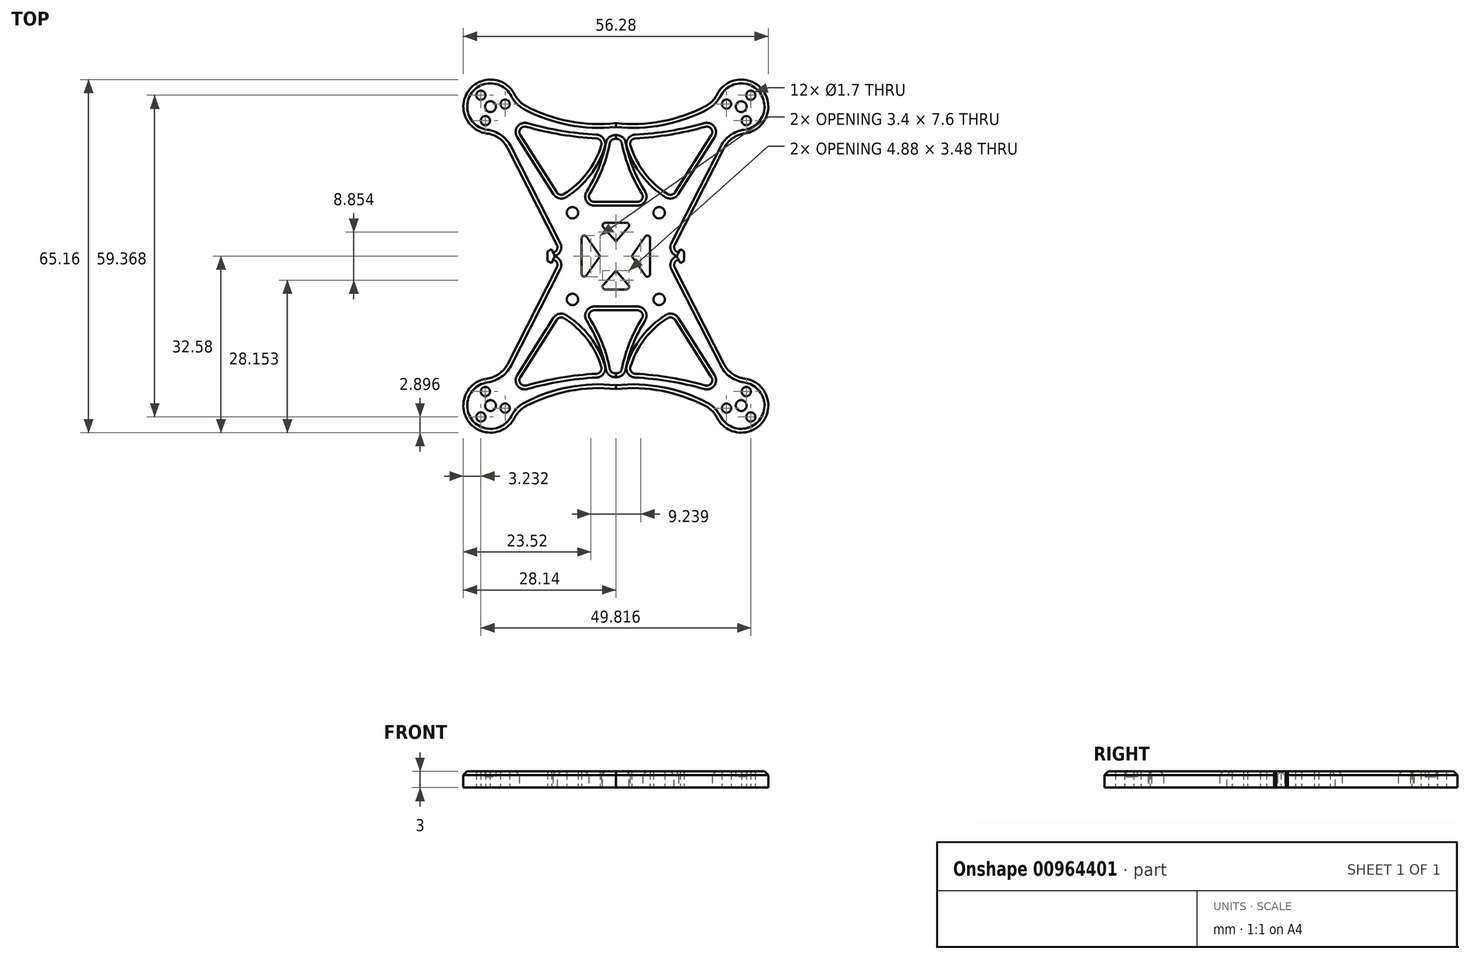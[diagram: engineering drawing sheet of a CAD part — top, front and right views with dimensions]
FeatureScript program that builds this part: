
annotation { "Feature Type Name" : "Feature", "Feature Type Description" : "" }
export const myFeature = defineFeature(function(context is Context, id is Id, definition is map)
    precondition{}
    {
        {
            var Q0;
            Q0=qCreatedBy(makeId("Top.planeOp"),FACE);
            var sketch = newSketch(context, id + "F0", { "sketchPlane" : qUnion([Q0])});
            skCircle(sketch, "E0", {"center": v(0, 0) * mm, "radius": 36 * mm, "construction": true});
            skLineSegment(sketch, "E1.bottom", {"start": v(8, -8) * mm, "end": v(-8, -8) * mm, "construction": true});
            skLineSegment(sketch, "E1.top", {"start": v(8, 8) * mm, "end": v(-8, 8) * mm, "construction": true});
            skLineSegment(sketch, "E1.left", {"start": v(8, -8) * mm, "end": v(8, 8) * mm, "construction": true});
            skLineSegment(sketch, "E1.right", {"start": v(-8, -8) * mm, "end": v(-8, 8) * mm, "construction": true});
            skCircle(sketch, "E2", {"center": v(-8, 8) * mm, "radius": 1.05 * mm});
            skCircle(sketch, "E3", {"center": v(8, 8) * mm, "radius": 1.05 * mm});
            skCircle(sketch, "E4", {"center": v(-8, -8) * mm, "radius": 1.05 * mm});
            skCircle(sketch, "E5", {"center": v(8, -8) * mm, "radius": 1.05 * mm});
            skLineSegment(sketch, "E6", {"start": v(0, 0) * mm, "end": v(50.6, 60.3) * mm, "construction": true});
            skPoint(sketch, "E7", {"position": v(23.14, 27.58) * mm});
            skCircle(sketch, "E8", {"center": v(23.14, 27.58) * mm, "radius": 1 * mm});
            skPoint(sketch, "E9", {"position": v(24.9, 29.68) * mm});
            skCircle(sketch, "E10", {"center": v(24.9, 29.68) * mm, "radius": 0.85 * mm});
            skCircle(sketch, "E11.1.0", {"center": v(20.43, 28.06) * mm, "radius": 0.85 * mm});
            skCircle(sketch, "E11.2.0", {"center": v(24.08, 25) * mm, "radius": 0.85 * mm});
            skCircle(sketch, "E12", {"center": v(23.14, 27.58) * mm, "radius": 20 * mm, "construction": true});
            skLineSegment(sketch, "E13.bottom", {"start": v(9.8, -10) * mm, "end": v(-9.8, -10) * mm});
            skLineSegment(sketch, "E13.top", {"start": v(9.8, 10) * mm, "end": v(-9.8, 10) * mm});
            skLineSegment(sketch, "E13.left", {"start": v(9.8, -10) * mm, "end": v(9.8, 10) * mm});
            skCircle(sketch, "E14", {"center": v(21.43, 25.54) * mm, "radius": 1.5 * mm, "construction": true});
            skLineSegment(sketch, "E15", {"start": v(23.14, 27.58) * mm, "end": v(9.8, 1.47) * mm, "construction": true});
            skLineSegment(sketch, "E16", {"start": v(9.8, 0) * mm, "end": v(22.09, 24.04) * mm});
            skCircle(sketch, "E17", {"center": v(23.14, 27.58) * mm, "radius": 5 * mm});
            skLineSegment(sketch, "E18", {"start": v(19.54, 25.37) * mm, "end": v(9.8, 10) * mm});
            skLineSegment(sketch, "E19", {"start": v(0, 10) * mm, "end": v(0, 0) * mm});
            skLineSegment(sketch, "E20", {"start": v(9.8, 0) * mm, "end": v(0, 0) * mm});
            skArc(sketch, "E21", {"start": v(0, 24.53) * mm, "mid": v(9.47, 25.07) * mm, "end": v(18.25, 28.64) * mm});
            skArc(sketch, "E22", {"start": v(0, 21.63) * mm, "mid": v(9.67, 22.35) * mm, "end": v(19.09, 24.65) * mm});
            skArc(sketch, "E23", {"start": v(2.36, 21.66) * mm, "mid": v(5.23, 15.44) * mm, "end": v(10.4, 10.96) * mm});
            skArc(sketch, "E24", {"start": v(0.97, 21.63) * mm, "mid": v(2.73, 15.53) * mm, "end": v(5.86, 10) * mm});
            skLineSegment(sketch, "E25", {"start": v(0, 24.53) * mm, "end": v(0, 21.63) * mm});
            skLineSegment(sketch, "E26", {"start": v(10.14, 0.66) * mm, "end": v(11.58, 0.66) * mm});
            skLineSegment(sketch, "E27", {"start": v(11.58, 0.66) * mm, "end": v(11.88, 1.25) * mm});
            skLineSegment(sketch, "E28", {"start": v(11.88, 1.25) * mm, "end": v(12.6, 0.88) * mm});
            skLineSegment(sketch, "E29", {"start": v(12.6, 0.88) * mm, "end": v(12.6, 0) * mm});
            skLineSegment(sketch, "E30", {"start": v(12.6, 0) * mm, "end": v(9.8, 0) * mm});
            skLineSegment(sketch, "E31", {"start": v(6.32, 4.9) * mm, "end": v(2.92, 0) * mm});
            skLineSegment(sketch, "E32", {"start": v(6.32, 4.9) * mm, "end": v(6.32, 0) * mm});
            skLineSegment(sketch, "E33", {"start": v(0, 6.17) * mm, "end": v(3.05, 6.17) * mm});
            skLineSegment(sketch, "E34", {"start": v(3.05, 6.17) * mm, "end": v(0, 2.69) * mm});
            skSolve(sketch);
        }
        {
            var Q0;
            {var subQ3=sQuery(id+"F0.wireOp",EDGE,"E21");Q0=makeQuery(id+"F0.imprint","IMPRINT",FACE,{"disambiguationData":[TD([[makeQuery(id+"F0.imprint","IMPRINT",EDGE,{"derivedFrom":subQ3}),-1.0]])]});}
            var Q1;
            Q1=makeQuery(id+"F0.imprint","IMPRINT",FACE,{"disambiguationData":[TD([[makeQuery(id+"F0.imprint","IMPRINT",EDGE,{"derivedFrom":sQuery(id+"F0.wireOp",EDGE,"E8")}),-1.0]])]});
            var Q2;
            {var subQ0=sQuery(id+"F0.wireOp",EDGE,"E17");var subQ1=sQuery(id+"F0.wireOp",EDGE,"E16");var subQ2=makeQuery(id+"F0.imprint","INTERSECT",VERTEX,{"derivedFrom":[subQ1,subQ0]});Q2=makeQuery(id+"F0.imprint","IMPRINT",FACE,{"disambiguationData":[TD([[makeQuery(id+"F0.imprint","IMPRINT",EDGE,{"disambiguationData":[TD([[subQ2,1.0]])],"derivedFrom":subQ0}),-1.0]])]});}
            var Q3;
            {var subQ0=sQuery(id+"F0.wireOp",EDGE,"E23");Q3=makeQuery(id+"F0.imprint","IMPRINT",FACE,{"disambiguationData":[TD([[makeQuery(id+"F0.imprint","IMPRINT",EDGE,{"derivedFrom":subQ0}),-1.0]])]});}
            var Q4;
            Q4=makeQuery(id+"F0.imprint","IMPRINT",FACE,{"disambiguationData":[TD([[makeQuery(id+"F0.imprint","IMPRINT",EDGE,{"derivedFrom":sQuery(id+"F0.wireOp",EDGE,"E3")}),-1.0]])]});
            var Q5;
            {var subQ0=sQuery(id+"F0.wireOp",EDGE,"E26");Q5=makeQuery(id+"F0.imprint","IMPRINT",FACE,{"disambiguationData":[TD([[makeQuery(id+"F0.imprint","IMPRINT",EDGE,{"derivedFrom":subQ0}),-1.0]])]});}
            extrude(context, id + "F1", {"entities" : qUnion([Q0, Q1, Q2, Q3, Q4, Q5]), "depth" : 3 * mm, "offsetDistance" : 25 * mm});
        }
        {
            var Q0;
            Q0=makeQuery(id+"F1.opExtrude","SWEPT_EDGE",EDGE,{"disambiguationData":[OSD([sQuery(id+"F0.wireOp",EDGE,"E17"),sQuery(id+"F0.wireOp",EDGE,"E21")])]});
            var Q1;
            Q1=makeQuery(id+"F1.opExtrude","SWEPT_EDGE",EDGE,{"disambiguationData":[OSD([sQuery(id+"F0.wireOp",EDGE,"E16"),sQuery(id+"F0.wireOp",EDGE,"E17")])]});
            fillet(context, id + "F2", {"entities" : qUnion([Q0, Q1]), "radius" : 5 * mm, "tangentPropagation" : true, "allowEdgeOverflow" : false});
        }
        {
            var Q0;
            Q0=makeQuery(id+"F1.opExtrude","SWEPT_EDGE",EDGE,{"disambiguationData":[OSD([sQuery(id+"F0.wireOp",EDGE,"E17"),sQuery(id+"F0.wireOp",EDGE,"E18")])]});
            var Q1;
            Q1=makeQuery(id+"F1.opExtrude","SWEPT_EDGE",EDGE,{"disambiguationData":[OSD([sQuery(id+"F0.wireOp",EDGE,"E17"),sQuery(id+"F0.wireOp",EDGE,"E22")])]});
            var Q2;
            Q2=makeQuery(id+"F1.opExtrude","SWEPT_EDGE",EDGE,{"disambiguationData":[OSD([sQuery(id+"F0.wireOp",EDGE,"E18"),sQuery(id+"F0.wireOp",EDGE,"E23")])]});
            var Q3;
            Q3=makeQuery(id+"F1.opExtrude","SWEPT_EDGE",EDGE,{"disambiguationData":[OSD([sQuery(id+"F0.wireOp",EDGE,"E22"),sQuery(id+"F0.wireOp",EDGE,"E23")])]});
            var Q4;
            Q4=makeQuery(id+"F1.opExtrude","SWEPT_EDGE",EDGE,{"disambiguationData":[OSD([sQuery(id+"F0.wireOp",EDGE,"E13.top"),sQuery(id+"F0.wireOp",EDGE,"E24")])]});
            var Q5;
            Q5=makeQuery(id+"F1.opExtrude","SWEPT_EDGE",EDGE,{"disambiguationData":[OSD([sQuery(id+"F0.wireOp",EDGE,"E22"),sQuery(id+"F0.wireOp",EDGE,"E24")])]});
            fillet(context, id + "F3", {"entities" : qUnion([Q0, Q1, Q2, Q3, Q4, Q5]), "radius" : 1 * mm, "tangentPropagation" : true, "allowEdgeOverflow" : false});
        }
        {
            var Q0;
            Q0=makeQuery(id+"F0.imprint","IMPRINT",FACE,{"disambiguationData":[TD([[makeQuery(id+"F0.imprint","IMPRINT",EDGE,{"derivedFrom":sQuery(id+"F0.wireOp",EDGE,"E8")}),1.0]])]});
            extrude(context, id + "F4", {"entities" : qUnion([Q0]), "operationType" : NewBodyOperationType.ADD, "depth" : 2 * mm, "offsetDistance" : 25 * mm});
        }
        {
            var Q0;
            Q0=makeQuery(id+"F1.opExtrude","SWEPT_EDGE",EDGE,{"disambiguationData":[OSD([sQuery(id+"F0.wireOp",EDGE,"E16"),sQuery(id+"F0.wireOp",EDGE,"E26")])]});
            fillet(context, id + "F5", {"entities" : qUnion([Q0]), "radius" : 1 * mm, "tangentPropagation" : true, "allowEdgeOverflow" : false});
        }
        {
            var Q0;
            Q0=makeQuery(id+"F1.opExtrude","SWEPT_EDGE",EDGE,{"disambiguationData":[OSD([sQuery(id+"F0.wireOp",EDGE,"E31"),sQuery(id+"F0.wireOp",EDGE,"E32")])]});
            var Q1;
            Q1=makeQuery(id+"F1.opExtrude","SWEPT_EDGE",EDGE,{"disambiguationData":[OSD([sQuery(id+"F0.wireOp",EDGE,"E33"),sQuery(id+"F0.wireOp",EDGE,"E34")])]});
            fillet(context, id + "F6", {"entities" : qUnion([Q0, Q1]), "radius" : .5 * mm, "tangentPropagation" : true, "allowEdgeOverflow" : false});
        }
        {
            var Q0;
            Q0=makeQuery(id+"F1.opExtrude","SWEPT_BODY",BODY,{"disambiguationData":[OSD([sQuery(id+"F0.wireOp",EDGE,"E3"),sQuery(id+"F0.wireOp",EDGE,"E8"),sQuery(id+"F0.wireOp",EDGE,"E10"),sQuery(id+"F0.wireOp",EDGE,"E11.1.0"),sQuery(id+"F0.wireOp",EDGE,"E11.2.0"),sQuery(id+"F0.wireOp",EDGE,"E13.top"),sQuery(id+"F0.wireOp",EDGE,"E16"),sQuery(id+"F0.wireOp",EDGE,"E17"),sQuery(id+"F0.wireOp",EDGE,"E18"),sQuery(id+"F0.wireOp",EDGE,"E19"),sQuery(id+"F0.wireOp",EDGE,"E20"),sQuery(id+"F0.wireOp",EDGE,"E21"),sQuery(id+"F0.wireOp",EDGE,"E22"),sQuery(id+"F0.wireOp",EDGE,"E23"),sQuery(id+"F0.wireOp",EDGE,"E24"),sQuery(id+"F0.wireOp",EDGE,"E25")])]});
            var Q1;
            Q1=qCreatedBy(makeId("Right.planeOp"),FACE);
            mirror(context, id + "F7", {"operationType" : NewBodyOperationType.ADD, "entities" : qUnion([Q0]), "mirrorPlane" : qUnion([Q1])});
        }
        {
            var Q0;
            Q0=makeQuery(id+"F1.opExtrude","SWEPT_BODY",BODY,{"disambiguationData":[OSD([sQuery(id+"F0.wireOp",EDGE,"E3"),sQuery(id+"F0.wireOp",EDGE,"E8"),sQuery(id+"F0.wireOp",EDGE,"E10"),sQuery(id+"F0.wireOp",EDGE,"E11.1.0"),sQuery(id+"F0.wireOp",EDGE,"E11.2.0"),sQuery(id+"F0.wireOp",EDGE,"E13.top"),sQuery(id+"F0.wireOp",EDGE,"E16"),sQuery(id+"F0.wireOp",EDGE,"E17"),sQuery(id+"F0.wireOp",EDGE,"E18"),sQuery(id+"F0.wireOp",EDGE,"E19"),sQuery(id+"F0.wireOp",EDGE,"E20"),sQuery(id+"F0.wireOp",EDGE,"E21"),sQuery(id+"F0.wireOp",EDGE,"E22"),sQuery(id+"F0.wireOp",EDGE,"E23"),sQuery(id+"F0.wireOp",EDGE,"E24"),sQuery(id+"F0.wireOp",EDGE,"E25")])]});
            var Q1;
            Q1=qCreatedBy(makeId("Front.planeOp"),FACE);
            mirror(context, id + "F8", {"operationType" : NewBodyOperationType.ADD, "entities" : qUnion([Q0]), "mirrorPlane" : qUnion([Q1])});
        }
        {
            var Q0;
            Q0=makeQuery(id+"F1.opExtrude","CAP_EDGE",EDGE,{"disambiguationData":[OSD([sQuery(id+"F0.wireOp",EDGE,"E18")])],"isStart":false});
            var Q1;
            Q1=makeQuery(id+"F1.opExtrude","CAP_EDGE",EDGE,{"disambiguationData":[OSD([sQuery(id+"F0.wireOp",EDGE,"E21")])],"isStart":false});
            var Q2;
            Q2=makeQuery(id+"F7.opPattern","COPY",EDGE,{"derivedFrom":makeQuery(id+"F1.opExtrude","CAP_EDGE",EDGE,{"disambiguationData":[OSD([sQuery(id+"F0.wireOp",EDGE,"E21")])],"isStart":false}),"instanceName":"1"});
            var Q3;
            Q3=makeQuery(id+"F8.opPattern","COPY",EDGE,{"derivedFrom":makeQuery(id+"F7.opPattern","COPY",EDGE,{"derivedFrom":makeQuery(id+"F1.opExtrude","CAP_EDGE",EDGE,{"disambiguationData":[OSD([sQuery(id+"F0.wireOp",EDGE,"E16")])],"isStart":false}),"instanceName":"1"}),"instanceName":"1"});
            var Q4;
            Q4=makeQuery(id+"F8.opPattern","COPY",EDGE,{"derivedFrom":makeQuery(id+"F1.opExtrude","CAP_EDGE",EDGE,{"disambiguationData":[OSD([sQuery(id+"F0.wireOp",EDGE,"E21")])],"isStart":false}),"instanceName":"1"});
            var Q5;
            Q5=makeQuery(id+"F7.opPattern","COPY",EDGE,{"derivedFrom":makeQuery(id+"F1.opExtrude","CAP_EDGE",EDGE,{"disambiguationData":[OSD([sQuery(id+"F0.wireOp",EDGE,"E23")])],"isStart":false}),"instanceName":"1"});
            var Q6;
            Q6=makeQuery(id+"F8.opPattern","COPY",EDGE,{"derivedFrom":makeQuery(id+"F7.opPattern","COPY",EDGE,{"derivedFrom":makeQuery(id+"F1.opExtrude","CAP_EDGE",EDGE,{"disambiguationData":[OSD([sQuery(id+"F0.wireOp",EDGE,"E23")])],"isStart":false}),"instanceName":"1"}),"instanceName":"1"});
            var Q7;
            Q7=makeQuery(id+"F8.opPattern","COPY",EDGE,{"derivedFrom":makeQuery(id+"F1.opExtrude","CAP_EDGE",EDGE,{"disambiguationData":[OSD([sQuery(id+"F0.wireOp",EDGE,"E23")])],"isStart":false}),"instanceName":"1"});
            var Q8;
            Q8=makeQuery(id+"F8.opPattern","COPY",EDGE,{"derivedFrom":makeQuery(id+"F1.opExtrude","CAP_EDGE",EDGE,{"disambiguationData":[OSD([sQuery(id+"F0.wireOp",EDGE,"E24")])],"isStart":false}),"instanceName":"1"});
            var Q9;
            {var subQ0=makeQuery(id+"F1.opExtrude","CAP_EDGE",EDGE,{"disambiguationData":[OSD([sQuery(id+"F0.wireOp",EDGE,"E13.top")])],"isStart":false});Q9=makeQuery(id+"F7.boolean.opBoolean","MERGE",EDGE,{"derivedFrom":[subQ0,makeQuery(id+"F7.opPattern","COPY",EDGE,{"derivedFrom":subQ0,"instanceName":"1"})]});}
            chamfer(context, id + "F9", {"entities" : qUnion([Q0, Q1, Q2, Q3, Q4, Q5, Q6, Q7, Q8, Q9]), "width" : 0.7 * mm, "tangentPropagation" : true});
        }
    });
